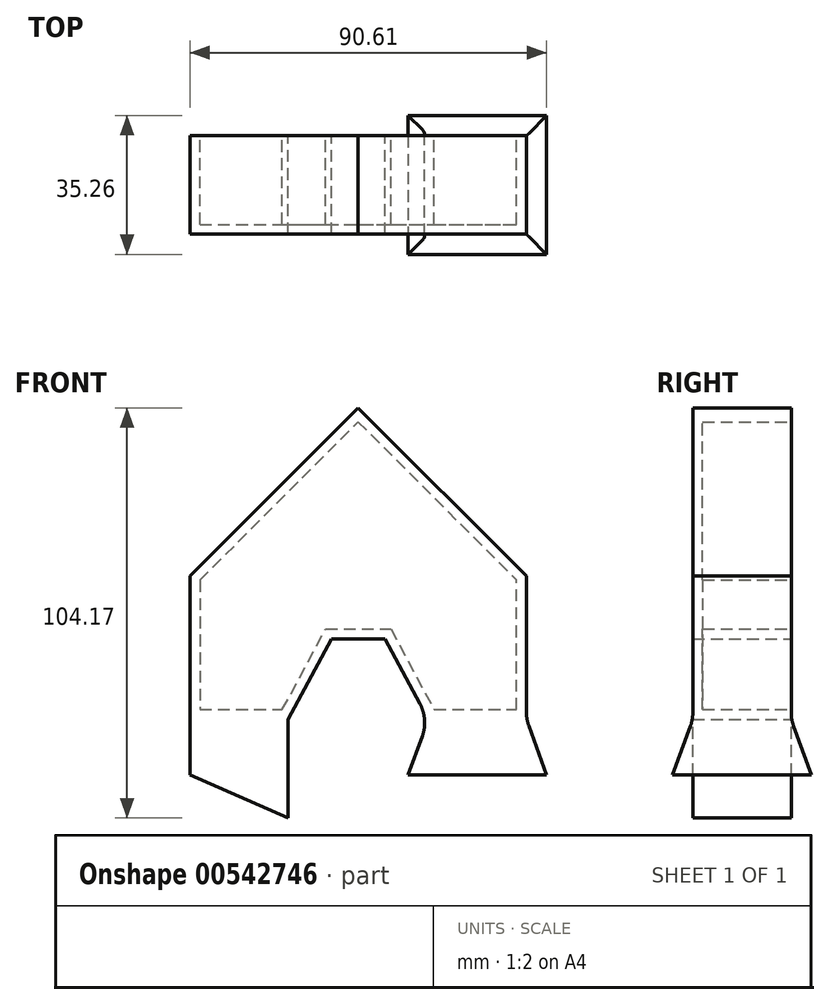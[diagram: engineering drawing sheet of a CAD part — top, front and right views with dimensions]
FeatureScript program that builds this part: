
annotation { "Feature Type Name" : "Feature", "Feature Type Description" : "" }
export const myFeature = defineFeature(function(context is Context, id is Id, definition is map)
    precondition{}
    {
        {
            var Q0;
            Q0=qCreatedBy(makeId("Front.planeOp"),FACE);
            var sketch = newSketch(context, id + "F0", { "sketchPlane" : qUnion([Q0])});
            skLineSegment(sketch, "E0", {"start": v(0, 0) * mm, "end": v(-85.48, 0) * mm});
            skLineSegment(sketch, "E1", {"start": v(-85.48, 0) * mm, "end": v(-85.48, -36.43) * mm});
            skLineSegment(sketch, "E2", {"start": v(-85.48, -36.43) * mm, "end": v(-60.56, -36.43) * mm});
            skLineSegment(sketch, "E3", {"start": v(-60.56, -36.43) * mm, "end": v(-49.52, -15.98) * mm});
            skLineSegment(sketch, "E4", {"start": v(-49.52, -15.98) * mm, "end": v(-35.97, -15.98) * mm});
            skLineSegment(sketch, "E5", {"start": v(-35.97, -15.98) * mm, "end": v(-24.93, -36.43) * mm});
            skLineSegment(sketch, "E6", {"start": v(-24.93, -36.43) * mm, "end": v(0, -36.43) * mm});
            skLineSegment(sketch, "E7", {"start": v(0, -36.43) * mm, "end": v(0, 0) * mm});
            skLineSegment(sketch, "E8", {"start": v(-85.48, 0) * mm, "end": v(-42.74, 42.74) * mm});
            skPoint(sketch, "E8.endSnap0", {"position": v(-42.74, 0) * mm});
            skLineSegment(sketch, "E9", {"start": v(-42.74, 42.74) * mm, "end": v(0, 0) * mm});
            skSolve(sketch);
        }
        {
            var Q0;
            Q0=makeQuery(id+"F0.imprint","IMPRINT",FACE,{"disambiguationData":[TD([[makeQuery(id+"F0.imprint","IMPRINT",EDGE,{"derivedFrom":sQuery(id+"F0.wireOp",EDGE,"E0")}),-1.0]])]});
            var Q1;
            Q1=makeQuery(id+"F0.imprint","IMPRINT",FACE,{"disambiguationData":[TD([[makeQuery(id+"F0.imprint","IMPRINT",EDGE,{"derivedFrom":sQuery(id+"F0.wireOp",EDGE,"E0")}),1.0]])]});
            extrude(context, id + "F1", {"entities" : qUnion([Q0, Q1]), "endBound" : BoundingType.SYMMETRIC, "depth" : 25 * mm, "offsetDistance" : 25 * mm});
        }
        {
            var Q0;
            Q0=makeQuery(id+"F1.opExtrude","SWEPT_FACE",FACE,{"disambiguationData":[OSD([sQuery(id+"F0.wireOp",EDGE,"E2")])]});
            var sketch = newSketch(context, id + "F2", { "sketchPlane" : qUnion([Q0])});
            skSolve(sketch);
        }
        {
            var Q0;
            {var subQ0=sQuery(id+"F0.wireOp",EDGE,"E2");Q0=makeQuery(id+"F4.boolean.opBoolean","MERGE",FACE,{"derivedFrom":[makeQuery(id+"F1.opExtrude","CAP_FACE",FACE,{"disambiguationData":[OSD([sQuery(id+"F0.wireOp",EDGE,"E1"),subQ0,sQuery(id+"F0.wireOp",EDGE,"E3"),sQuery(id+"F0.wireOp",EDGE,"E4"),sQuery(id+"F0.wireOp",EDGE,"E5"),sQuery(id+"F0.wireOp",EDGE,"E6"),sQuery(id+"F0.wireOp",EDGE,"E7"),sQuery(id+"F0.wireOp",EDGE,"E8"),sQuery(id+"F0.wireOp",EDGE,"E9")])],"isStart":true}),makeQuery(id+"F4.opExtrude","SWEPT_FACE",FACE,{"disambiguationData":[OSD([subQ0]),TDD([makeQuery(id+"F2.imprint","IMPRINT",EDGE,{"derivedFrom":makeQuery(id+"F1.opExtrude","CAP_EDGE",EDGE,{"disambiguationData":[OSD([subQ0])],"isStart":true})})])]})]});}
            shell(context, id + "F3", {"entities" : qUnion([Q0]), "thickness" : 2.5 * mm});
        }
        {
            var Q0;
            {var subQ0=sQuery(id+"F0.wireOp",EDGE,"E2");Q0=makeQuery(id+"F2.imprint","IMPRINT",FACE,{"disambiguationData":[TD([[makeQuery(id+"F2.imprint","IMPRINT",EDGE,{"derivedFrom":makeQuery(id+"F1.opExtrude","CAP_EDGE",EDGE,{"disambiguationData":[OSD([subQ0])],"isStart":true})}),1.0]])]});}
            extrude(context, id + "F4", {"entities" : qUnion([Q0]), "operationType" : NewBodyOperationType.ADD, "depth" : 25 * mm, "offsetDistance" : 25 * mm});
        }
        {
            var Q0;
            Q0=makeQuery(id+"F1.opExtrude","SWEPT_FACE",FACE,{"disambiguationData":[OSD([sQuery(id+"F0.wireOp",EDGE,"E6")])]});
            var sketch = newSketch(context, id + "F5", { "sketchPlane" : qUnion([Q0])});
            skSolve(sketch);
        }
        {
            var Q0;
            {var subQ0=sQuery(id+"F0.wireOp",EDGE,"E6");Q0=makeQuery(id+"F5.imprint","IMPRINT",FACE,{"disambiguationData":[TD([[makeQuery(id+"F5.imprint","IMPRINT",EDGE,{"derivedFrom":makeQuery(id+"F1.opExtrude","CAP_EDGE",EDGE,{"disambiguationData":[OSD([subQ0])],"isStart":true})}),1.0]])]});}
            extrude(context, id + "F6", {"entities" : qUnion([Q0]), "operationType" : NewBodyOperationType.ADD, "depth" : 14.1 * mm, "offsetDistance" : 25 * mm, "hasDraft" : true, "draftAngle" : 20 * degree});
        }
        {
            var Q0;
            {var subQ0=sQuery(id+"F0.wireOp",EDGE,"E6");var subQ1=makeQuery(id+"F1.opExtrude","CAP_EDGE",EDGE,{"disambiguationData":[OSD([subQ0])],"isStart":false});Q0=makeQuery(id+"F6.boolean.opBoolean","MERGE",EDGE,{"derivedFrom":[subQ1,makeQuery(id+"F6.opExtrude","CAP_EDGE",EDGE,{"disambiguationData":[OSD([subQ0]),TDD([makeQuery(id+"F5.imprint","IMPRINT",EDGE,{"derivedFrom":subQ1})])],"isStart":true})]});}
            var Q1;
            {var subQ0=sQuery(id+"F0.wireOp",EDGE,"E6");var subQ1=sQuery(id+"F0.wireOp",EDGE,"E5");Q1=makeQuery(id+"F6.boolean.opBoolean","MERGE",EDGE,{"derivedFrom":[makeQuery(id+"F1.opExtrude","SWEPT_EDGE",EDGE,{"disambiguationData":[OSD([subQ1,subQ0])]}),makeQuery(id+"F6.opExtrude","CAP_EDGE",EDGE,{"disambiguationData":[OSD([subQ1,subQ0])],"isStart":true})]});}
            var Q2;
            {var subQ0=sQuery(id+"F0.wireOp",EDGE,"E6");var subQ1=makeQuery(id+"F1.opExtrude","CAP_EDGE",EDGE,{"disambiguationData":[OSD([subQ0])],"isStart":true});Q2=makeQuery(id+"F6.boolean.opBoolean","MERGE",EDGE,{"derivedFrom":[subQ1,makeQuery(id+"F6.opExtrude","CAP_EDGE",EDGE,{"disambiguationData":[OSD([subQ0]),TDD([makeQuery(id+"F5.imprint","IMPRINT",EDGE,{"derivedFrom":subQ1})])],"isStart":true})]});}
            var Q3;
            {var subQ0=sQuery(id+"F0.wireOp",EDGE,"E7");var subQ1=sQuery(id+"F0.wireOp",EDGE,"E6");Q3=makeQuery(id+"F6.boolean.opBoolean","MERGE",EDGE,{"derivedFrom":[makeQuery(id+"F1.opExtrude","SWEPT_EDGE",EDGE,{"disambiguationData":[OSD([subQ1,subQ0])]}),makeQuery(id+"F6.opExtrude","CAP_EDGE",EDGE,{"disambiguationData":[OSD([subQ1,subQ0])],"isStart":true})]});}
            fillet(context, id + "F7", {"entities" : qUnion([Q0, Q1, Q2, Q3]), "radius" : 10 * mm, "tangentPropagation" : true, "allowEdgeOverflow" : false});
        }
        {
            var Q0;
            {var subQ0=sQuery(id+"F0.wireOp",EDGE,"E2");Q0=makeQuery(id+"F4.boolean.opBoolean","MERGE",FACE,{"derivedFrom":[makeQuery(id+"F1.opExtrude","CAP_FACE",FACE,{"disambiguationData":[OSD([sQuery(id+"F0.wireOp",EDGE,"E1"),subQ0,sQuery(id+"F0.wireOp",EDGE,"E3"),sQuery(id+"F0.wireOp",EDGE,"E4"),sQuery(id+"F0.wireOp",EDGE,"E5"),sQuery(id+"F0.wireOp",EDGE,"E6"),sQuery(id+"F0.wireOp",EDGE,"E7"),sQuery(id+"F0.wireOp",EDGE,"E8"),sQuery(id+"F0.wireOp",EDGE,"E9")])],"isStart":false}),makeQuery(id+"F4.opExtrude","SWEPT_FACE",FACE,{"disambiguationData":[OSD([subQ0]),TDD([makeQuery(id+"F2.imprint","IMPRINT",EDGE,{"derivedFrom":makeQuery(id+"F1.opExtrude","CAP_EDGE",EDGE,{"disambiguationData":[OSD([subQ0])],"isStart":false})})])]})]});}
            var sketch = newSketch(context, id + "F8", { "sketchPlane" : qUnion([Q0])});
            skLineSegment(sketch, "E10", {"start": v(-85.48, -50.53) * mm, "end": v(-60.56, -61.43) * mm});
            skSolve(sketch);
        }
        {
            var Q0;
            {var subQ0=sQuery(id+"F8.wireOp",EDGE,"E10");Q0=makeQuery(id+"F8.imprint","IMPRINT",FACE,{"disambiguationData":[TD([[makeQuery(id+"F8.imprint","IMPRINT",EDGE,{"derivedFrom":subQ0}),-1.0]])]});}
            extrude(context, id + "F9", {"entities" : qUnion([Q0]), "operationType" : NewBodyOperationType.REMOVE, "oppositeDirection" : true, "depth" : 68.5 * mm, "offsetDistance" : 25 * mm});
        }
    });
